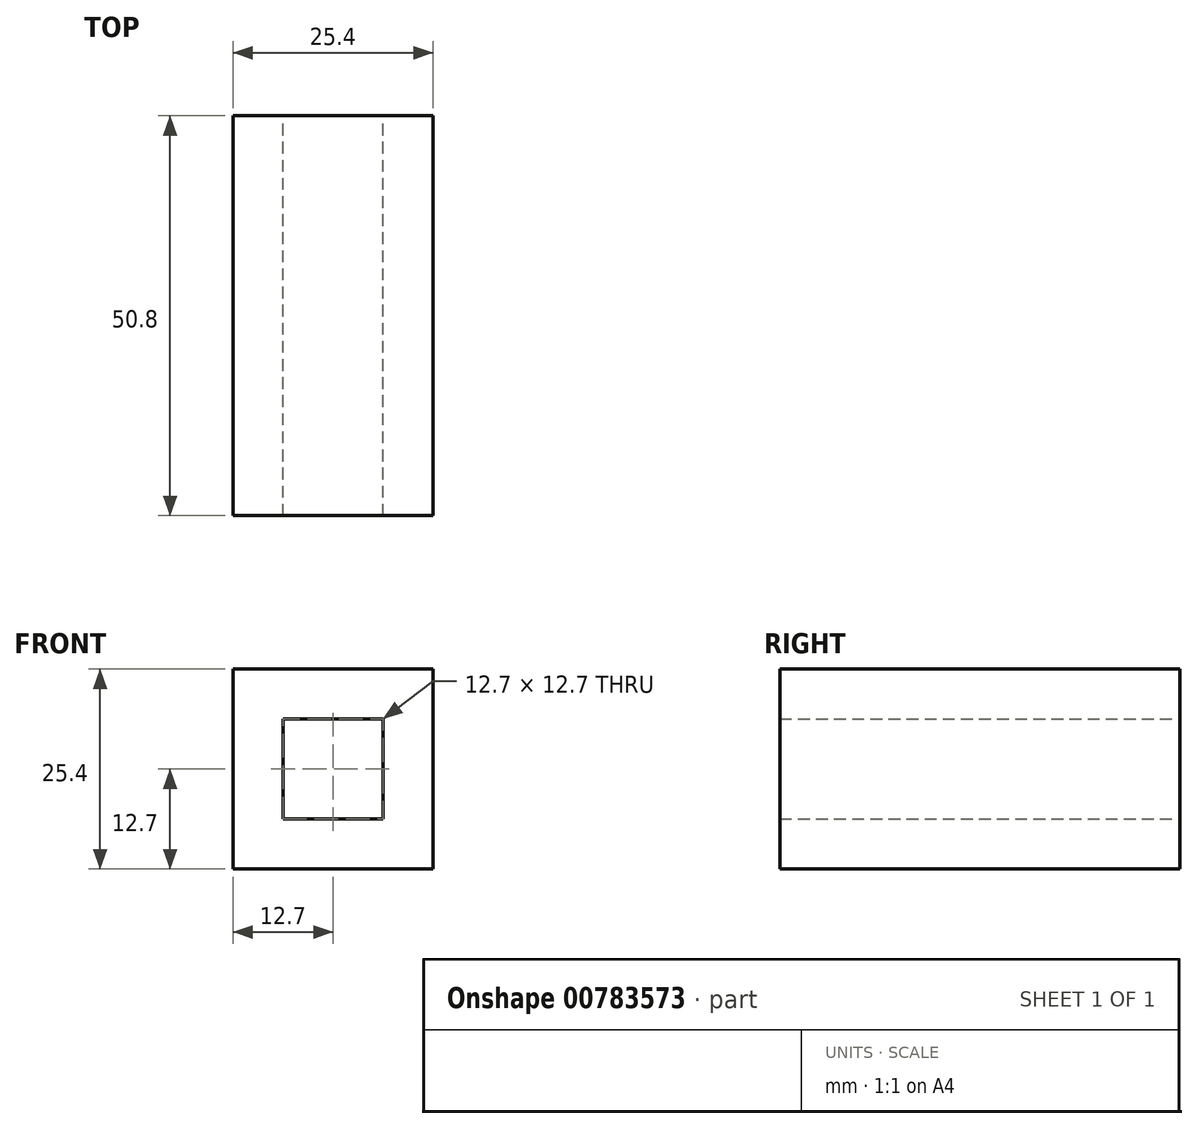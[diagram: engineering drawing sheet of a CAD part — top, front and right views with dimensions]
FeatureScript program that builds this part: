
annotation { "Feature Type Name" : "Feature", "Feature Type Description" : "" }
export const myFeature = defineFeature(function(context is Context, id is Id, definition is map)
    precondition{}
    {
        {
            var Q0;
            Q0=qCreatedBy(makeId("Front.planeOp"),FACE);
            var sketch = newSketch(context, id + "F0", { "sketchPlane" : qUnion([Q0])});
            skLineSegment(sketch, "E0.bottom", {"start": v(-12.7, 12.7) * mm, "end": v(12.7, 12.7) * mm});
            skLineSegment(sketch, "E0.top", {"start": v(-12.7, -12.7) * mm, "end": v(12.7, -12.7) * mm});
            skLineSegment(sketch, "E0.left", {"start": v(-12.7, 12.7) * mm, "end": v(-12.7, -12.7) * mm});
            skLineSegment(sketch, "E0.right", {"start": v(12.7, 12.7) * mm, "end": v(12.7, -12.7) * mm});
            skPoint(sketch, "E1", {"position": v(0, 0) * mm});
            skPoint(sketch, "E1.positionSnap0", {"position": v(-12.7, 0) * mm});
            skPoint(sketch, "E1.positionSnap1", {"position": v(0, 12.7) * mm});
            skLineSegment(sketch, "E2.bottom", {"start": v(-6.35, 6.35) * mm, "end": v(6.35, 6.35) * mm});
            skLineSegment(sketch, "E2.top", {"start": v(-6.35, -6.35) * mm, "end": v(6.35, -6.35) * mm});
            skLineSegment(sketch, "E2.left", {"start": v(-6.35, 6.35) * mm, "end": v(-6.35, -6.35) * mm});
            skLineSegment(sketch, "E2.right", {"start": v(6.35, 6.35) * mm, "end": v(6.35, -6.35) * mm});
            skPoint(sketch, "E3.positionSnap0", {"position": v(-6.35, 0) * mm});
            skPoint(sketch, "E3.positionSnap1", {"position": v(0, 6.35) * mm});
            skSolve(sketch);
        }
        {
            var Q0;
            Q0=makeQuery(id+"F0.imprint","IMPRINT",FACE,{"disambiguationData":[TD([[makeQuery(id+"F0.imprint","IMPRINT",EDGE,{"derivedFrom":sQuery(id+"F0.wireOp",EDGE,"E0.bottom")}),-1.0]])]});
            extrude(context, id + "F1", {"entities" : qUnion([Q0]), "depth" : 50.8 * mm, "offsetDistance" : 25.4 * mm});
        }
    });
